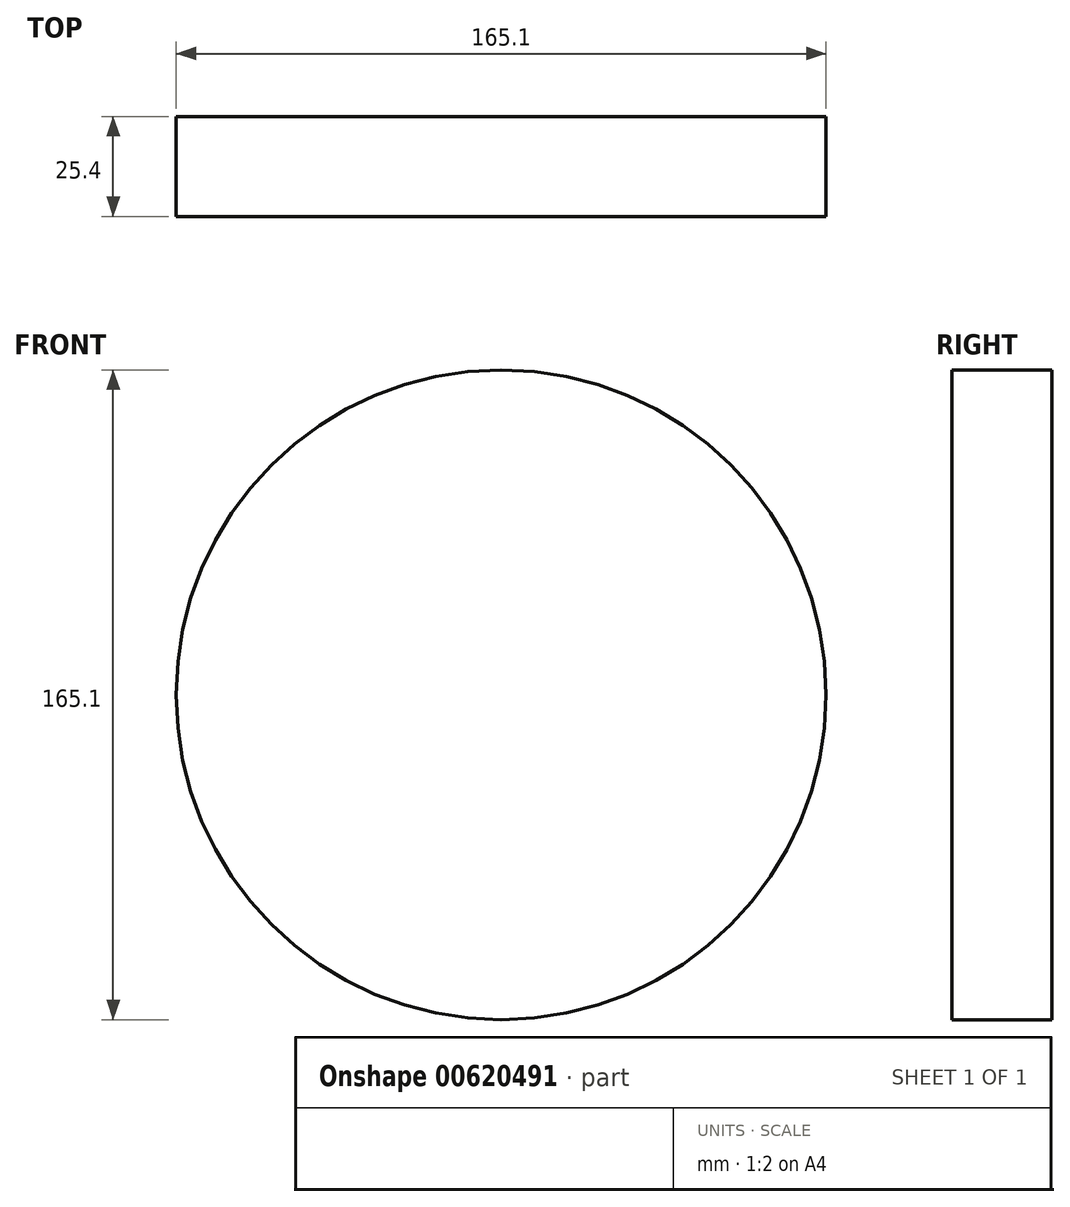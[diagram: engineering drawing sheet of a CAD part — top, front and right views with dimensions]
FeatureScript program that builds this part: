
annotation { "Feature Type Name" : "Feature", "Feature Type Description" : "" }
export const myFeature = defineFeature(function(context is Context, id is Id, definition is map)
    precondition{}
    {
        {
            var Q0;
            Q0=qCreatedBy(makeId("Front.planeOp"),FACE);
            var sketch = newSketch(context, id + "F0", { "sketchPlane" : qUnion([Q0])});
            skCircle(sketch, "E0", {"center": v(0, 0) * mm, "radius": 82.55 * mm});
            skSolve(sketch);
        }
        {
            var Q0;
            Q0 = qSketchRegion(id + "F0", true);
            extrude(context, id + "F1", {"entities" : qUnion([Q0]), "depth" : 25.4 * mm, "offsetDistance" : 25.4 * mm});
        }
    });
